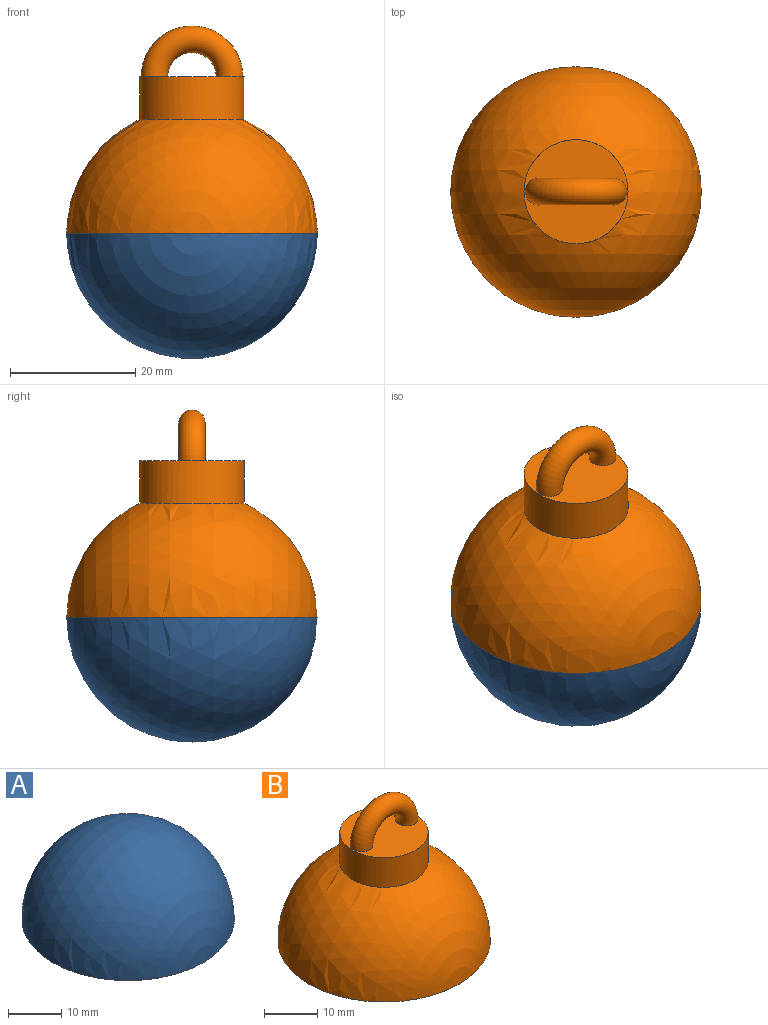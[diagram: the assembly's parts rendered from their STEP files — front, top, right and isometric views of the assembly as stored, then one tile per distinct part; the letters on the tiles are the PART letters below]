
ASSEMBLY  parts=2 mates=1
PART A: 2 faces, bbox 40x40x20 mm
  f0: sphere r=20mm, area 2513.3mm2, adj f1
  f1: plane 40x40mm, normal (0,0,-1), area 1256.6mm2, adj f0
PART B: 5 faces, bbox 40x40x33.8 mm
  f0: sphere r=20mm, area 2286.1mm2, adj f1,f2
  f1: plane 40x40mm, normal (0,0,-1), area 1256.6mm2, adj f0
  f2: cylinder r=8.31mm len=16.62mm, axis (0,0,-1), area 355.4mm2, adj f0,f3
  f3: plane 16.62x16.62mm, normal (0,0,1), area 188.6mm2, adj f2,f4
  f4: torus R=5.99mm, axis (0,1,0), area 250.7mm2, adj f3
PLACE A rot(axis=(0,1,0),180deg) t=(36.43,6.75,2.81)mm
PLACE B t=(36.43,6.75,2.81)mm
MATE fastened B.f2 <-> A.f1  axis (0,0,-1) through (36.43,6.75,2.81)mm
